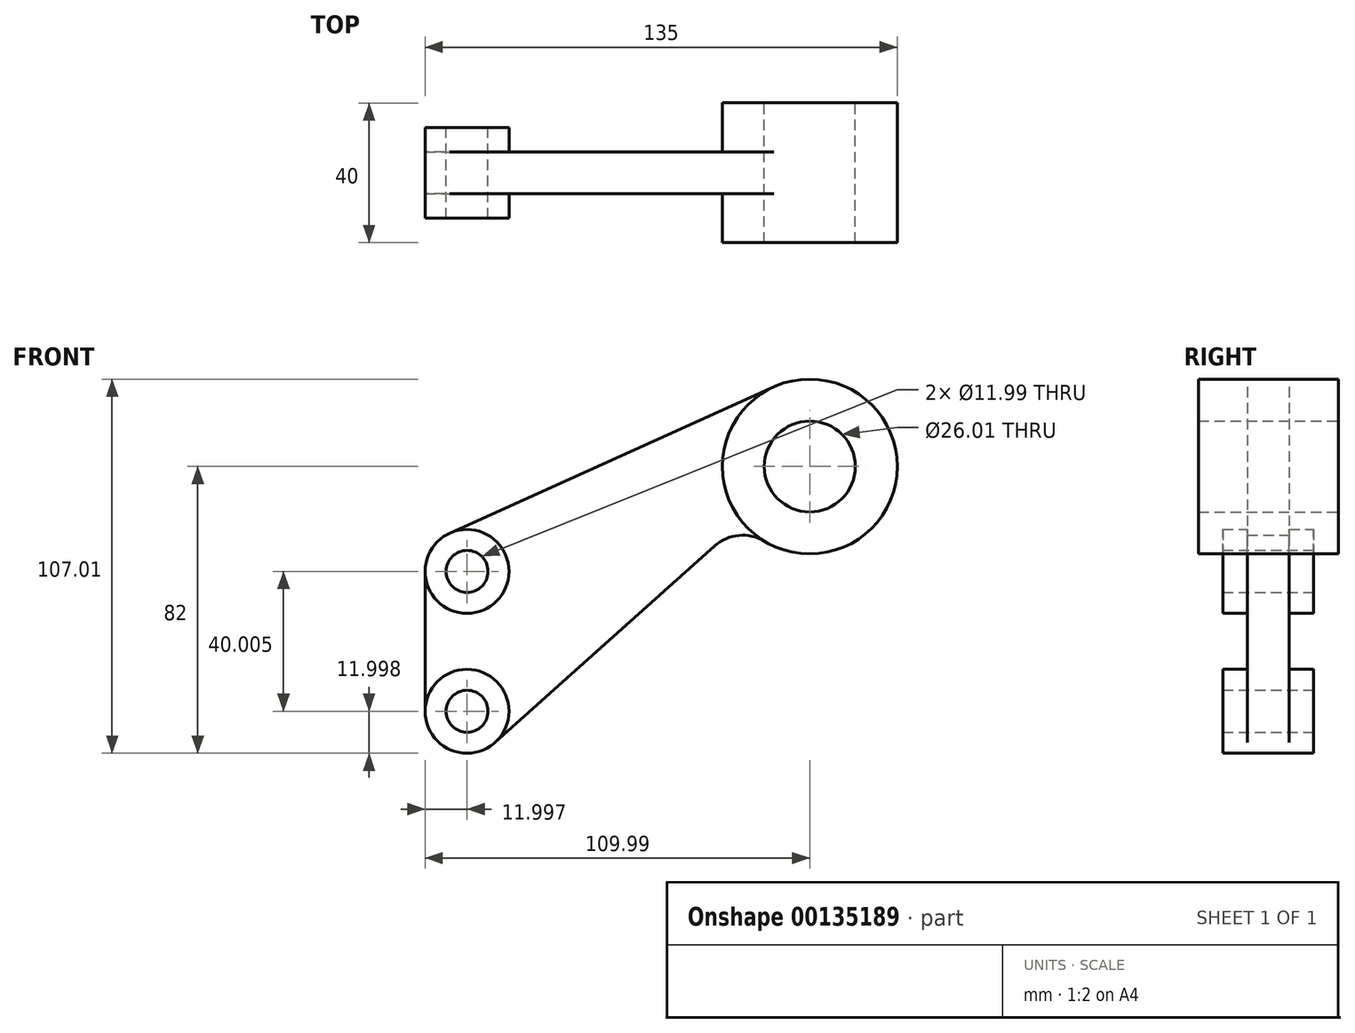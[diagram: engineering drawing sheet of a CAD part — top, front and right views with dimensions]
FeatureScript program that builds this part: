
annotation { "Feature Type Name" : "Feature", "Feature Type Description" : "" }
export const myFeature = defineFeature(function(context is Context, id is Id, definition is map)
    precondition{}
    {
        {
            var Q0;
            Q0=qCreatedBy(makeId("Front.planeOp"),FACE);
            var sketch = newSketch(context, id + "F0", { "sketchPlane" : qUnion([Q0])});
            skCircle(sketch, "E0", {"center": v(0, 0) * mm, "radius": 13 * mm});
            skCircle(sketch, "E1", {"center": v(0, 0) * mm, "radius": 25 * mm});
            skCircle(sketch, "E2", {"center": v(-98, -30) * mm, "radius": 6 * mm});
            skCircle(sketch, "E3", {"center": v(-98, -30) * mm, "radius": 12 * mm});
            skCircle(sketch, "E4", {"center": v(-98, -70) * mm, "radius": 6 * mm});
            skCircle(sketch, "E5", {"center": v(-98, -70) * mm, "radius": 12 * mm});
            skLineSegment(sketch, "E6", {"start": v(-10.3, 22.79) * mm, "end": v(-102.93, -19.06) * mm});
            skLineSegment(sketch, "E7", {"start": v(-110, -30) * mm, "end": v(-110, -70) * mm});
            skArc(sketch, "E8", {"start": v(-12.95, -21.4) * mm, "mid": v(-20.27, -19.71) * mm, "end": v(-27.15, -22.71) * mm});
            skLineSegment(sketch, "E9", {"start": v(-90, -78.95) * mm, "end": v(-27.15, -22.71) * mm});
            skSolve(sketch);
        }
        {
            var Q0;
            {var subQ0=sQuery(id+"F0.wireOp",EDGE,"E6");Q0=makeQuery(id+"F0.imprint","IMPRINT",FACE,{"disambiguationData":[TD([[makeQuery(id+"F0.imprint","IMPRINT",EDGE,{"derivedFrom":subQ0}),1.0]])]});}
            extrude(context, id + "F1", {"entities" : qUnion([Q0]), "endBound" : BoundingType.SYMMETRIC, "depth" : 12 * mm});
        }
        {
            var Q0;
            Q0=makeQuery(id+"F0.imprint","IMPRINT",FACE,{"disambiguationData":[TD([[makeQuery(id+"F0.imprint","IMPRINT",EDGE,{"derivedFrom":sQuery(id+"F0.wireOp",EDGE,"E0")}),-1.0]])]});
            extrude(context, id + "F2", {"entities" : qUnion([Q0]), "operationType" : NewBodyOperationType.ADD, "endBound" : BoundingType.SYMMETRIC, "depth" : 40 * mm});
        }
        {
            var Q0;
            Q0=makeQuery(id+"F0.imprint","IMPRINT",FACE,{"disambiguationData":[TD([[makeQuery(id+"F0.imprint","IMPRINT",EDGE,{"derivedFrom":sQuery(id+"F0.wireOp",EDGE,"E2")}),-1.0]])]});
            var Q1;
            Q1=makeQuery(id+"F0.imprint","IMPRINT",FACE,{"disambiguationData":[TD([[makeQuery(id+"F0.imprint","IMPRINT",EDGE,{"derivedFrom":sQuery(id+"F0.wireOp",EDGE,"E4")}),-1.0]])]});
            extrude(context, id + "F3", {"entities" : qUnion([Q0, Q1]), "operationType" : NewBodyOperationType.ADD, "endBound" : BoundingType.SYMMETRIC, "depth" : 26 * mm});
        }
    });
